# Revit family: Magnuson-Slide-Coat_Tree-1
name_source: partatom
category: Furniture
revit_build: Autodesk Revit 2016 (Build: 20150220_1215(x64)
units: mm (PartAtom-declared; Revit-internal decimal feet)

## family parameters
Always vertical = Yes
Cut with Voids When Loaded = No
OmniClass Number = 23.40.20.00
OmniClass Title = General Furniture and Specialties
Room Calculation Point = No
Shared = No
Work Plane-Based = No

## types (3) — shared parameters
Assembly Code = E2020200
Base Finish = MAG-Paint Steel White
Cap Finish = MAG-Paint Steel White
Height = 67 5/8"
Hook Finish = MAG-Plastic White
Keynote = 12500
Low Emitting Finish = Yes
Low Emitting Material = Yes
Manufacturer = Magnuson Group
Post Finish = MAG-Paint Steel White
Revit File Built By = https://servex-us.com
Salvage or Reuse = No
Type Comments = Coat Trees
URL = www.magnusongroup.com
zero-valued in all types: Percentage of Recycled Content

## per-type parameters (varying)
| type | #Hook | B1 | B2 | B3 | Depth | Description | Dist Hook | Width |
| SLIDE G1 | 2 | Yes | No | No | 11 13/16" | Single painted steel coat tree with 6 plastic hooks | 5 29/32" | 11 13/16" |
| SLIDE G2 | 2 | No | Yes | No | 9 13/16" | Double painted steel coat tree with 12 plastic hooks | 4 59/64" | 21 41/64" |
| SLIDE G3 | 3 | No | No | Yes | 9 13/16" | Triple painted steel coat tree with 18 plastic hooks | 4 59/64" | 33 15/32" |

note: column(s) folded — value = type name in every type: Model

## geometry (parser evidence)
native form markers: Sweep x7
no freeform markers — native parametric forms only
